# Revit family: Pump_Commercial-Effluent-Zoeller-264_Non_Automatic_Series
name_source: partatom
category: Mechanical Equipment
revit_build: Autodesk Revit 2014 (Build: 20130308_1515(x64)
units: mm (PartAtom-declared; Revit-internal decimal feet)

## types (2) — shared parameters
Apparent Load = 1081 VA
Cooling = Oil Filled
Cord Length = 180"
Cord Type = UL listed cord and plug
Default Elevation = 0"
Description = Submersible sewage/effluent or dewatering pumps.
Discharge Diameter = 2" NPT
Discharge Height = 6 1/2"
Discharge Radius = 1"
Height = 14 3/4"
Hertz = 60
Impeller = Engineered Plastic
Impeller Type = Non-clogging vortex
Installation Type = Floor Mounted
Insulation = Class B
Length = 11 3/8"
Manufacturer = Zoeller
Material = Cast Iron-Zoeller-Powder Coated Epoxy
Max. Flow @ 5' = 90 GPM
Max. Water Temp. = 130 °F
Maximum Head = 18'
Motor = 4/10 HP
Motor Thermal Protection = Auto reset thermal overload
O-Rings and Cover Gasket = Neoprene
Operation = Non Automatic
Phase = 1 Ph
Price = Prices may vary. Please consult Manufacturer Representative for most up-to-date price list.
Product Page URL = http://www.zoellerpumps.com
RPM = 1725
Single Piggyback Switch = No
Solid Handling = 2" Spherical Solids
Type = Permanent Split Capacitor
Type Comments = Automatic or Non-Automatic available
URL = http://www.zoellerengprod.com
Warranty Information = 36 Months (Limited)
Waste Connection = Yes
Width = 13 5/32"

## per-type parameters (varying)
| type | Amps | Model | Voltage |
| N264 - 115V 1Ph | 9 A | N264 | 115 V |
| E264 - 230V 1Ph | 5 A | E264 | 230 V |

## geometry (parser evidence)
native form markers: Sweep x2
no freeform markers — native parametric forms only
